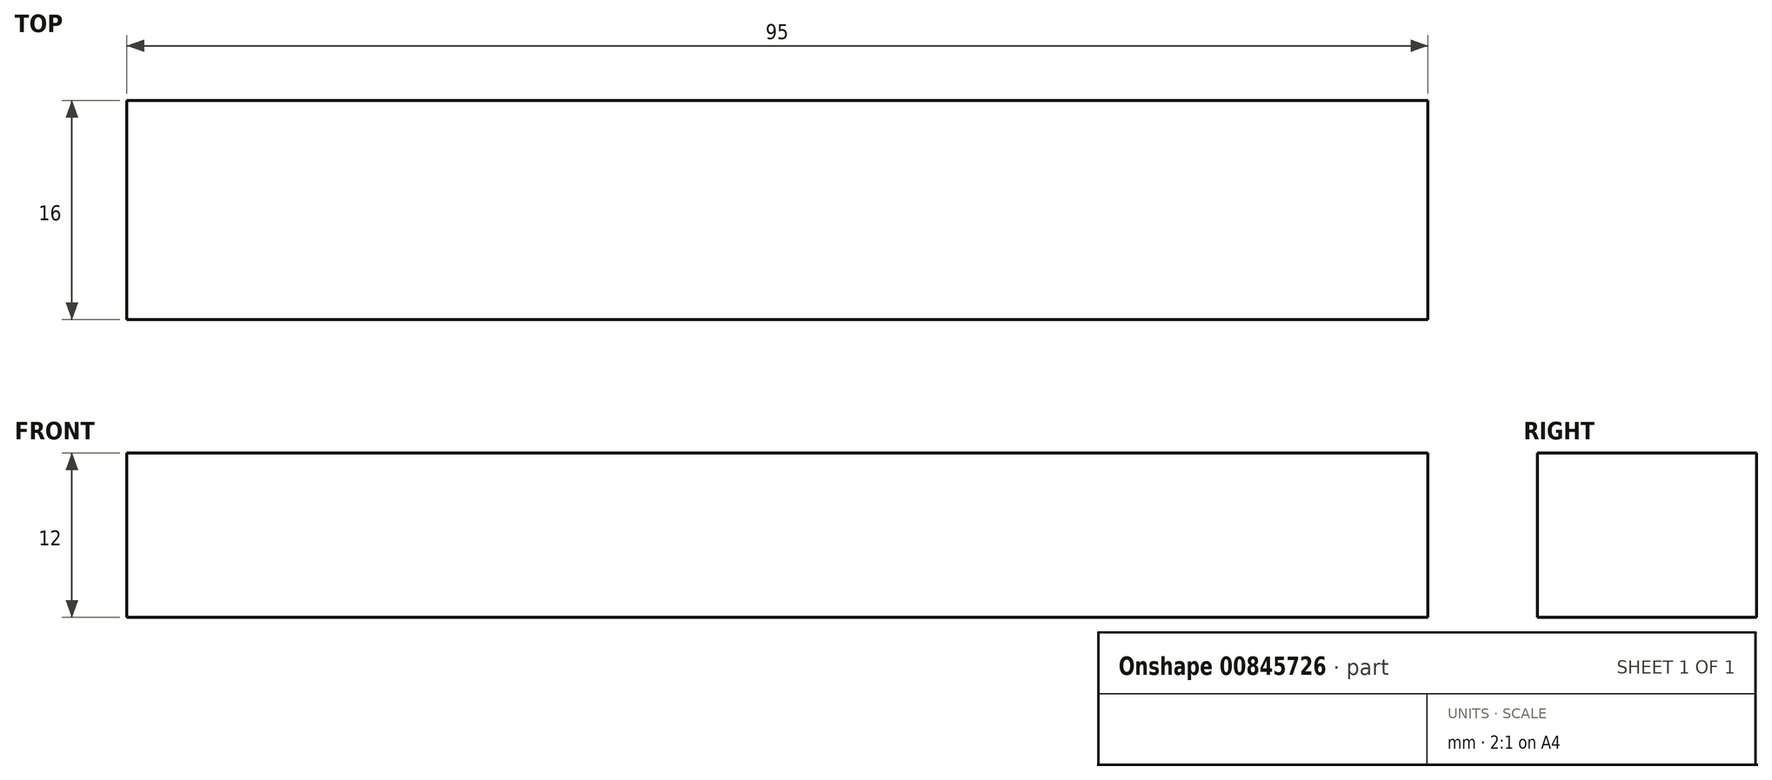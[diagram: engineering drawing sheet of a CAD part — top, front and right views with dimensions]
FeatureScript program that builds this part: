
annotation { "Feature Type Name" : "Feature", "Feature Type Description" : "" }
export const myFeature = defineFeature(function(context is Context, id is Id, definition is map)
    precondition{}
    {
        {
            var Q0;
            Q0=qCreatedBy(makeId("Right.planeOp"),FACE);
            var sketch = newSketch(context, id + "F0", { "sketchPlane" : qUnion([Q0])});
            skLineSegment(sketch, "E0", {"start": v(0, 0) * mm, "end": v(0, 12) * mm});
            skLineSegment(sketch, "E1", {"start": v(0, 0) * mm, "end": v(-16, 0) * mm});
            skLineSegment(sketch, "E2", {"start": v(0, 12) * mm, "end": v(-16, 12) * mm});
            skLineSegment(sketch, "E3", {"start": v(-16, 12) * mm, "end": v(-16, 0) * mm});
            skSolve(sketch);
        }
        {
            var Q0;
            Q0 = qSketchRegion(id + "F0", true);
            extrude(context, id + "F1", {"entities" : qUnion([Q0]), "depth" : 95 * mm, "offsetDistance" : 25 * mm});
        }
    });
